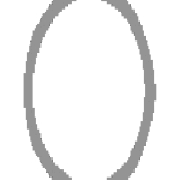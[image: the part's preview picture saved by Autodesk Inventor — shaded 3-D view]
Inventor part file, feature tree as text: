
AUTODESK INVENTOR PART (.ipt)
format: ipt  version: 2021 (Build 250183000, 183)  size: 146,944 bytes
history: native  units: in
note: dims shown in document units (in); Inventor stores cm internally (conversion verified against a paired STEP export)
features: other x5, sketch x2, sweep x1, plane x1
ambient origin geometry x8: Origin, YZ Plane, XZ Plane, XY Plane, X Axis, Y Axis, Z Axis, Center Point
bodies: Solid1 (feature_tree), Body (feature_tree)
feature tree (9):
  other  "Driven Length"
  other  "Frame Generator"
  other  "Start Plane"
  other  "End Plane"
  sweep  "Sweep Path"
  other  "Orientation Work Plane"
  sketch  "Sketch2"  dims[d0=1.0in d1=0.065in]
  plane  "Work Plane3"
  sketch  "Sketch3"  dims[d2=1.1738in d4=-0.0in d5=1.1738in d8=90.0deg d9=1.1738in d10=0.0in d11=0.0in]
